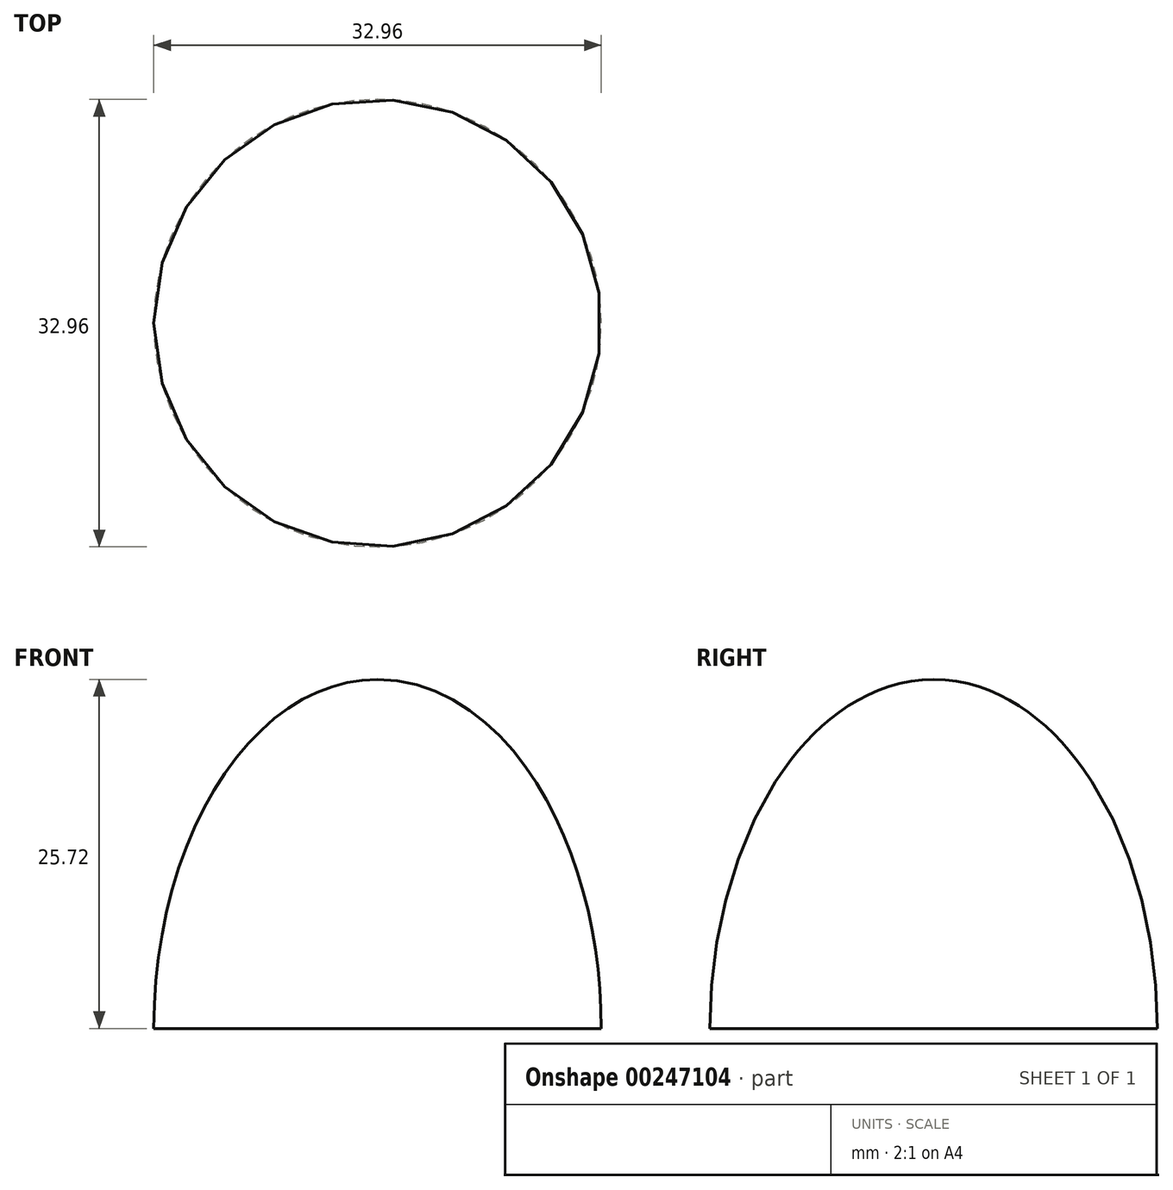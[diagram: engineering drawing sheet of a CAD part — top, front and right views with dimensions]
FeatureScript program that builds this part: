
annotation { "Feature Type Name" : "Feature", "Feature Type Description" : "" }
export const myFeature = defineFeature(function(context is Context, id is Id, definition is map)
    precondition{}
    {
        {
            var Q0;
            Q0=qCreatedBy(makeId("Front.planeOp"),FACE);
            var sketch = newSketch(context, id + "F0", { "sketchPlane" : qUnion([Q0])});
            skEllipse(sketch, "E0", {"center": v(0, 0) * mm, "majorRadius": 26.58 * mm, "minorRadius": 16.93 * mm, "majorAxis": v(0, 1)});
            skLineSegment(sketch, "E1", {"start": v(-16.93, 0) * mm, "end": v(16.93, 0) * mm});
            skSolve(sketch);
        }
        {
            var Q0;
            {var subQ0=sQuery(id+"F0.wireOp",EDGE,"E1");Q0=makeQuery(id+"F0.imprint","IMPRINT",FACE,{"disambiguationData":[TD([[makeQuery(id+"F0.imprint","IMPRINT",EDGE,{"derivedFrom":subQ0}),-1.0]])]});}
            var sketch = newSketch(context, id + "F1", { "sketchPlane" : qUnion([Q0])});
            skPoint(sketch, "E2.start.orphan", {"position": v(-16.76, 0) * mm});
            skLineSegment(sketch, "E3", {"start": v(-16.76, 0) * mm, "end": v(0, 0) * mm});
            skEllipticalArc(sketch, "E4", {});
            skLineSegment(sketch, "E5", {"start": v(0, 0) * mm, "end": v(0, 25.72) * mm});
            const initialGuessF1  = {"E4": [0, 0, 0, 1, 0.025715263560414314, 0.016475161277458402, 0, 1.5707963267948966]};
            skSetInitialGuess(sketch, initialGuessF1);
            skSolve(sketch);
        }
        {
            var Q0;
            Q0 = qSketchRegion(id + "F1", true);
            var Q1;
            Q1=sQuery(id+"F1.wireOp",EDGE,"E5");
            revolve(context, id + "F2", {"entities" : qUnion([Q0]), "axis" : qUnion([Q1]), "revolveType" : RevolveType.FULL});
        }
    });
